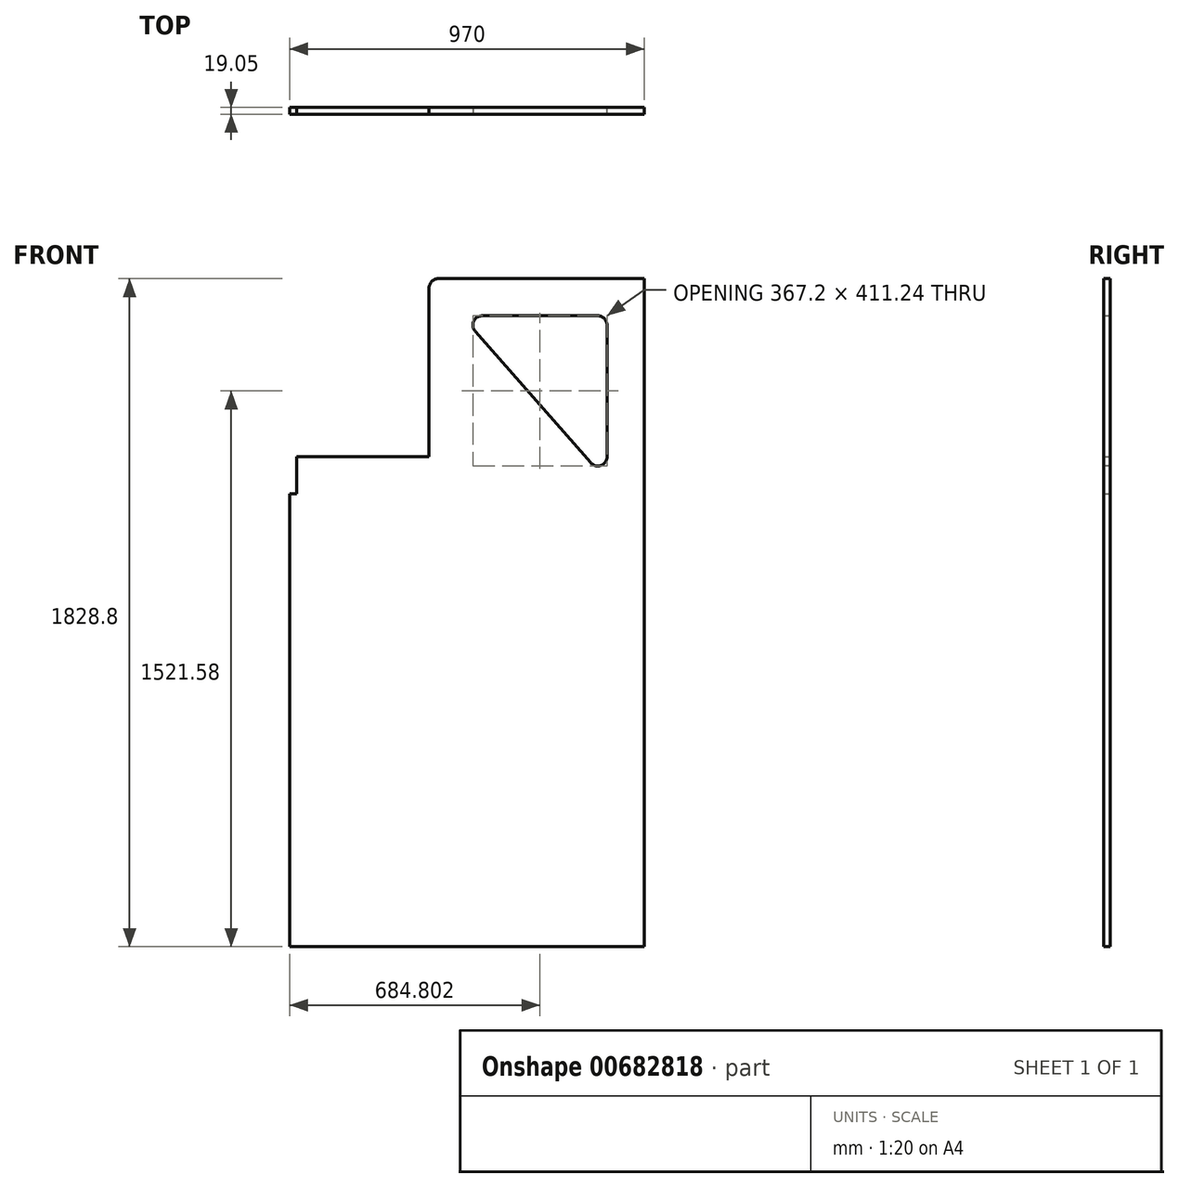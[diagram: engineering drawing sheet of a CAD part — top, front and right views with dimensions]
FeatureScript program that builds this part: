
annotation { "Feature Type Name" : "Feature", "Feature Type Description" : "" }
export const myFeature = defineFeature(function(context is Context, id is Id, definition is map)
    precondition{}
    {
        {
            var Q0;
            Q0=qCreatedBy(makeId("Front.planeOp"),FACE);
            var sketch = newSketch(context, id + "F0", { "sketchPlane" : qUnion([Q0])});
            skLineSegment(sketch, "E0.bottom", {"start": v(0, 0) * mm, "end": v(-970, 0) * mm});
            skLineSegment(sketch, "E0.left", {"start": v(0, 0) * mm, "end": v(0, 1158.24) * mm});
            skLineSegment(sketch, "E0.right", {"start": v(-970, 0) * mm, "end": v(-970, 1239.52) * mm});
            skLineSegment(sketch, "E1", {"start": v(-589, 1828.8) * mm, "end": v(0, 1158.24) * mm, "construction": true});
            skLineSegment(sketch, "E2", {"start": v(-970, 1117.6) * mm, "end": v(-589, 1117.6) * mm, "construction": true});
            skLineSegment(sketch, "E3", {"start": v(-589, 1117.6) * mm, "end": v(-589, 894.08) * mm, "construction": true});
            skLineSegment(sketch, "E4", {"start": v(-589, 894.08) * mm, "end": v(-392.67, 894.08) * mm, "construction": true});
            skLineSegment(sketch, "E5", {"start": v(-392.67, 894.08) * mm, "end": v(-392.67, 670.56) * mm, "construction": true});
            skLineSegment(sketch, "E6", {"start": v(-392.67, 670.56) * mm, "end": v(-196.33, 670.56) * mm, "construction": true});
            skLineSegment(sketch, "E7", {"start": v(-196.33, 670.56) * mm, "end": v(-196.33, 447.04) * mm, "construction": true});
            skLineSegment(sketch, "E8", {"start": v(-196.33, 447.04) * mm, "end": v(0, 447.04) * mm, "construction": true});
            skLineSegment(sketch, "E9", {"start": v(0, 223.52) * mm, "end": v(196.33, 223.52) * mm, "construction": true});
            skLineSegment(sketch, "E10", {"start": v(196.33, 223.52) * mm, "end": v(196.33, 0) * mm, "construction": true});
            skLineSegment(sketch, "E11", {"start": v(-98.17, 447.04) * mm, "end": v(-98.17, 223.52) * mm, "construction": true});
            skLineSegment(sketch, "E12", {"start": v(-98.17, 223.52) * mm, "end": v(0, 223.52) * mm, "construction": true});
            skLineSegment(sketch, "E13", {"start": v(-589, 1117.6) * mm, "end": v(-392.67, 894.08) * mm, "construction": true});
            skLineSegment(sketch, "E14", {"start": v(-589, 1828.8) * mm, "end": v(0, 1828.8) * mm});
            skLineSegment(sketch, "E15", {"start": v(0, 1828.8) * mm, "end": v(0, 1158.24) * mm});
            skLineSegment(sketch, "E16", {"start": v(-499.76, 1727.2) * mm, "end": v(-101.6, 1727.2) * mm});
            skLineSegment(sketch, "E17", {"start": v(-101.6, 1727.2) * mm, "end": v(-101.6, 1273.9) * mm});
            skLineSegment(sketch, "E18", {"start": v(-101.6, 1273.9) * mm, "end": v(-499.76, 1727.2) * mm});
            skLineSegment(sketch, "E19", {"start": v(-589, 1828.8) * mm, "end": v(-589, 1341.12) * mm});
            skLineSegment(sketch, "E20", {"start": v(-589, 1341.12) * mm, "end": v(-950.95, 1341.12) * mm});
            skLineSegment(sketch, "E21", {"start": v(-950.95, 1341.12) * mm, "end": v(-950.95, 1239.52) * mm});
            skLineSegment(sketch, "E22", {"start": v(-950.95, 1239.52) * mm, "end": v(-970, 1239.52) * mm});
            skSolve(sketch);
        }
        {
            var Q0;
            Q0=qSketchRegion(id+"F0",true);
            extrude(context, id + "F1", {"entities" : qUnion([Q0]), "depth" : 19.05 * mm, "offsetDistance" : 25.4 * mm});
        }
        {
            var Q0;
            Q0=makeQuery(id+"F1.opExtrude","SWEPT_EDGE",EDGE,{"disambiguationData":[OSD([sQuery(id+"F0.wireOp",EDGE,"E16"),sQuery(id+"F0.wireOp",EDGE,"E18")])]});
            var Q1;
            Q1=makeQuery(id+"F1.opExtrude","SWEPT_EDGE",EDGE,{"disambiguationData":[OSD([sQuery(id+"F0.wireOp",EDGE,"E16"),sQuery(id+"F0.wireOp",EDGE,"E17")])]});
            var Q2;
            Q2=makeQuery(id+"F1.opExtrude","SWEPT_EDGE",EDGE,{"disambiguationData":[OSD([sQuery(id+"F0.wireOp",EDGE,"E17"),sQuery(id+"F0.wireOp",EDGE,"E18")])]});
            var Q3;
            Q3=makeQuery(id+"F1.opExtrude","SWEPT_EDGE",EDGE,{"disambiguationData":[OSD([sQuery(id+"F0.wireOp",EDGE,"E14"),sQuery(id+"F0.wireOp",EDGE,"E19")])]});
            fillet(context, id + "F2", {"entities" : qUnion([Q0, Q1, Q2, Q3]), "radius" : 25.4 * mm, "tangentPropagation" : true, "allowEdgeOverflow" : false});
        }
    });
